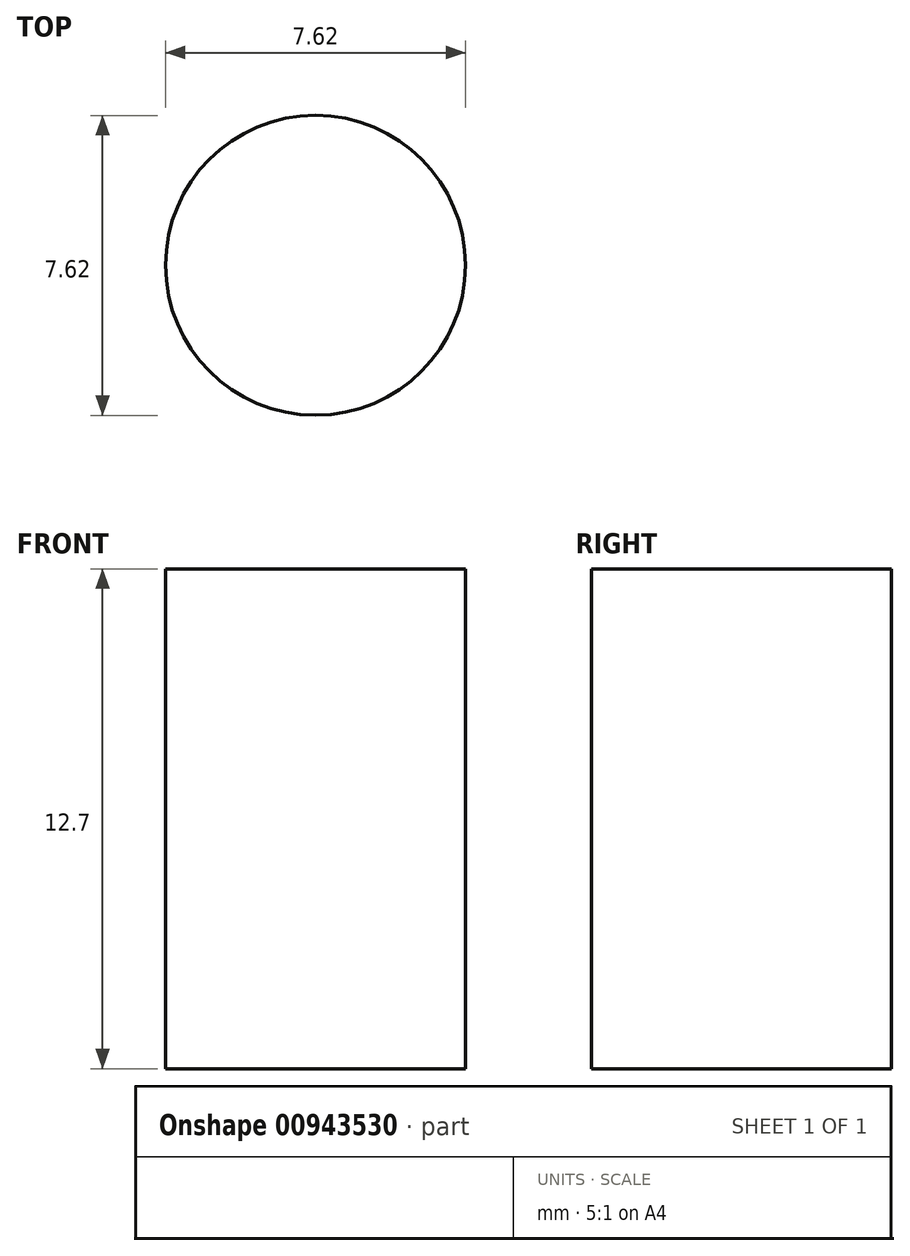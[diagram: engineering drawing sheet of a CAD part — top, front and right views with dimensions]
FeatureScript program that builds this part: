
annotation { "Feature Type Name" : "Feature", "Feature Type Description" : "" }
export const myFeature = defineFeature(function(context is Context, id is Id, definition is map)
    precondition{}
    {
        {
            var Q0;
            Q0=qCreatedBy(makeId("Top.planeOp"),FACE);
            var sketch = newSketch(context, id + "F0", { "sketchPlane" : qUnion([Q0])});
            skCircle(sketch, "E0", {"center": v(-22.03, 15.76) * mm, "radius": 3.81 * mm});
            skSolve(sketch);
        }
        {
            var Q0;
            Q0=makeQuery(id+"F0.imprint","IMPRINT",FACE,{"disambiguationData":[TD([[makeQuery(id+"F0.imprint","IMPRINT",EDGE,{"derivedFrom":sQuery(id+"F0.wireOp",EDGE,"E0")}),1.0]])]});
            extrude(context, id + "F1", {"entities" : qUnion([Q0]), "depth" : 12.7 * mm, "offsetDistance" : 25.4 * mm});
        }
    });
